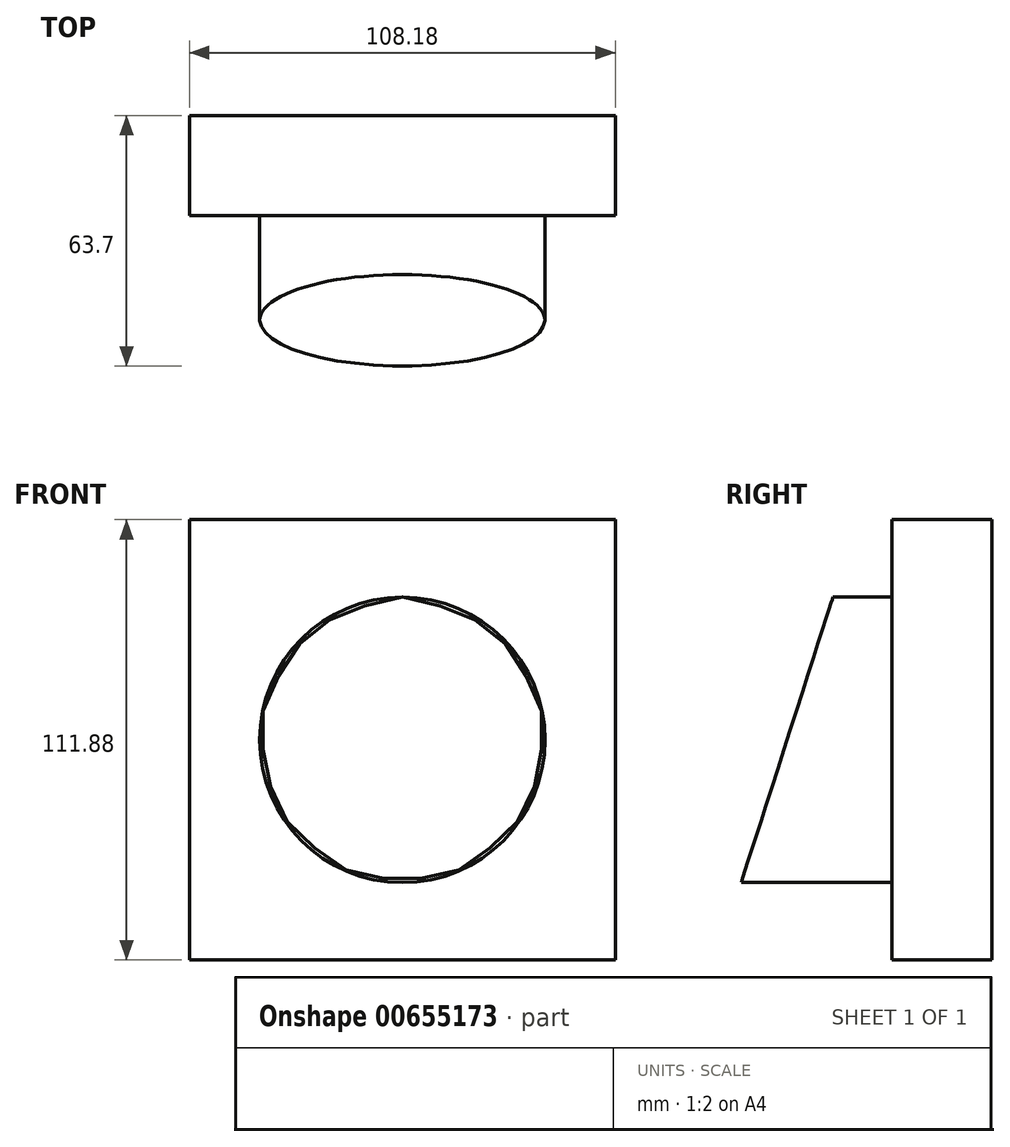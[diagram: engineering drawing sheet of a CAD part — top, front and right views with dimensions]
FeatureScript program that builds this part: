
annotation { "Feature Type Name" : "Feature", "Feature Type Description" : "" }
export const myFeature = defineFeature(function(context is Context, id is Id, definition is map)
    precondition{}
    {
        {
            var Q0;
            Q0=qCreatedBy(makeId("Front.planeOp"),FACE);
            var sketch = newSketch(context, id + "F0", { "sketchPlane" : qUnion([Q0])});
            skLineSegment(sketch, "E0.bottom", {"start": v(54.1, -55.94) * mm, "end": v(-54.1, -55.94) * mm});
            skLineSegment(sketch, "E0.top", {"start": v(54.1, 55.94) * mm, "end": v(-54.1, 55.94) * mm});
            skLineSegment(sketch, "E0.left", {"start": v(54.1, -55.94) * mm, "end": v(54.1, 55.94) * mm});
            skLineSegment(sketch, "E0.right", {"start": v(-54.1, -55.94) * mm, "end": v(-54.1, 55.94) * mm});
            skPoint(sketch, "E0.middle", {"position": v(0, 0) * mm});
            skSolve(sketch);
        }
        {
            var Q0;
            Q0 = qSketchRegion(id + "F0", true);
            extrude(context, id + "F1", {"entities" : qUnion([Q0]), "depth" : 25.4 * mm, "offsetDistance" : 25.4 * mm});
        }
        {
            var Q0;
            Q0=makeQuery(id+"F1.opExtrude","CAP_FACE",FACE,{"disambiguationData":[OSD([sQuery(id+"F0.wireOp",EDGE,"E0.bottom"),sQuery(id+"F0.wireOp",EDGE,"E0.top"),sQuery(id+"F0.wireOp",EDGE,"E0.left"),sQuery(id+"F0.wireOp",EDGE,"E0.right")])],"isStart":false});
            var sketch = newSketch(context, id + "F2", { "sketchPlane" : qUnion([Q0])});
            skCircle(sketch, "E1", {"center": v(0, 0) * mm, "radius": 36.26 * mm});
            skSolve(sketch);
        }
        {
            var Q0;
            Q0 = qSketchRegion(id + "F2", true);
            extrude(context, id + "F3", {"entities" : qUnion([Q0]), "operationType" : NewBodyOperationType.ADD, "depth" : 50.8 * mm, "offsetDistance" : 25.4 * mm});
        }
        {
            var Q0;
            Q0=qCreatedBy(makeId("Right.planeOp"),FACE);
            var sketch = newSketch(context, id + "F4", { "sketchPlane" : qUnion([Q0])});
            skLineSegment(sketch, "E2", {"start": v(-76.18, 54.48) * mm, "end": v(-34.57, 54.48) * mm});
            skLineSegment(sketch, "E3", {"start": v(-34.57, 54.48) * mm, "end": v(-76.18, -75.13) * mm});
            skLineSegment(sketch, "E4.bottom", {"start": v(-76.18, 54.48) * mm, "end": v(-82.46, 54.48) * mm});
            skLineSegment(sketch, "E4.top", {"start": v(-76.18, -75.28) * mm, "end": v(-82.46, -75.28) * mm});
            skLineSegment(sketch, "E4.left", {"start": v(-76.18, -75.13) * mm, "end": v(-76.18, -75.28) * mm});
            skLineSegment(sketch, "E4.right", {"start": v(-82.46, 54.48) * mm, "end": v(-82.46, -75.28) * mm});
            skSolve(sketch);
        }
        {
            var Q0;
            Q0 = qSketchRegion(id + "F4", true);
            extrude(context, id + "F5", {"entities" : qUnion([Q0]), "operationType" : NewBodyOperationType.REMOVE, "endBound" : BoundingType.SYMMETRIC, "oppositeDirection" : true, "depth" : 109.47 * mm, "offsetDistance" : 25.4 * mm});
        }
    });
